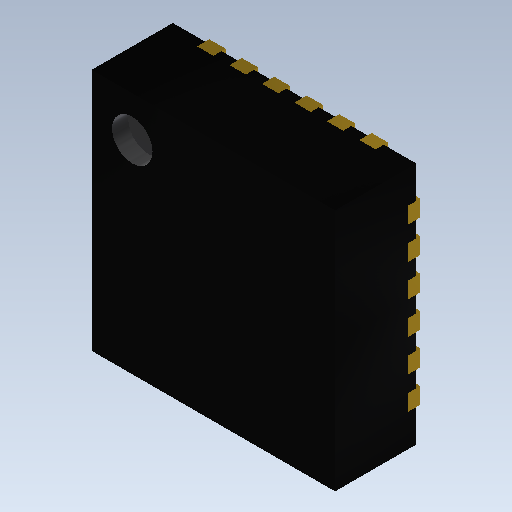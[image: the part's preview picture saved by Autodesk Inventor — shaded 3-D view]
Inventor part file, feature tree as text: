
AUTODESK INVENTOR PART (.ipt)
format: ipt  version: 2020.3 (Build 243373000, 373)  size: 383,488 bytes
history: native  units: mm
features: extrude x7, sketch x7, other x1
ambient origin geometry x8: Origin, YZ Plane, XZ Plane, XY Plane, X Axis, Y Axis, Z Axis, Center Point
bodies: Body1 (feature_tree)
feature tree (15):
  other  "Твердое тело1"
  extrude  "Выдавливание1"  Depth=3.0mm
  extrude  "Выдавливание2"  Depth=1.0mm TaperAngle=0.0deg
  extrude  "Выдавливание3"  Depth=0.5mm
  extrude  "Выдавливание4"  Depth=0.5mm
  extrude  "Выдавливание5"  Depth=0.5mm
  extrude  "Выдавливание6"  Depth=0.2mm TaperAngle=0.0deg
  extrude  "Выдавливание7"  Depth=0.3mm
  sketch  "Эскиз1"
  sketch  "Эскиз2"
  sketch  "Эскиз3"
  sketch  "Эскиз4"
  sketch  "Эскиз5"
  sketch  "Эскиз6"
  sketch  "Эскиз7"
